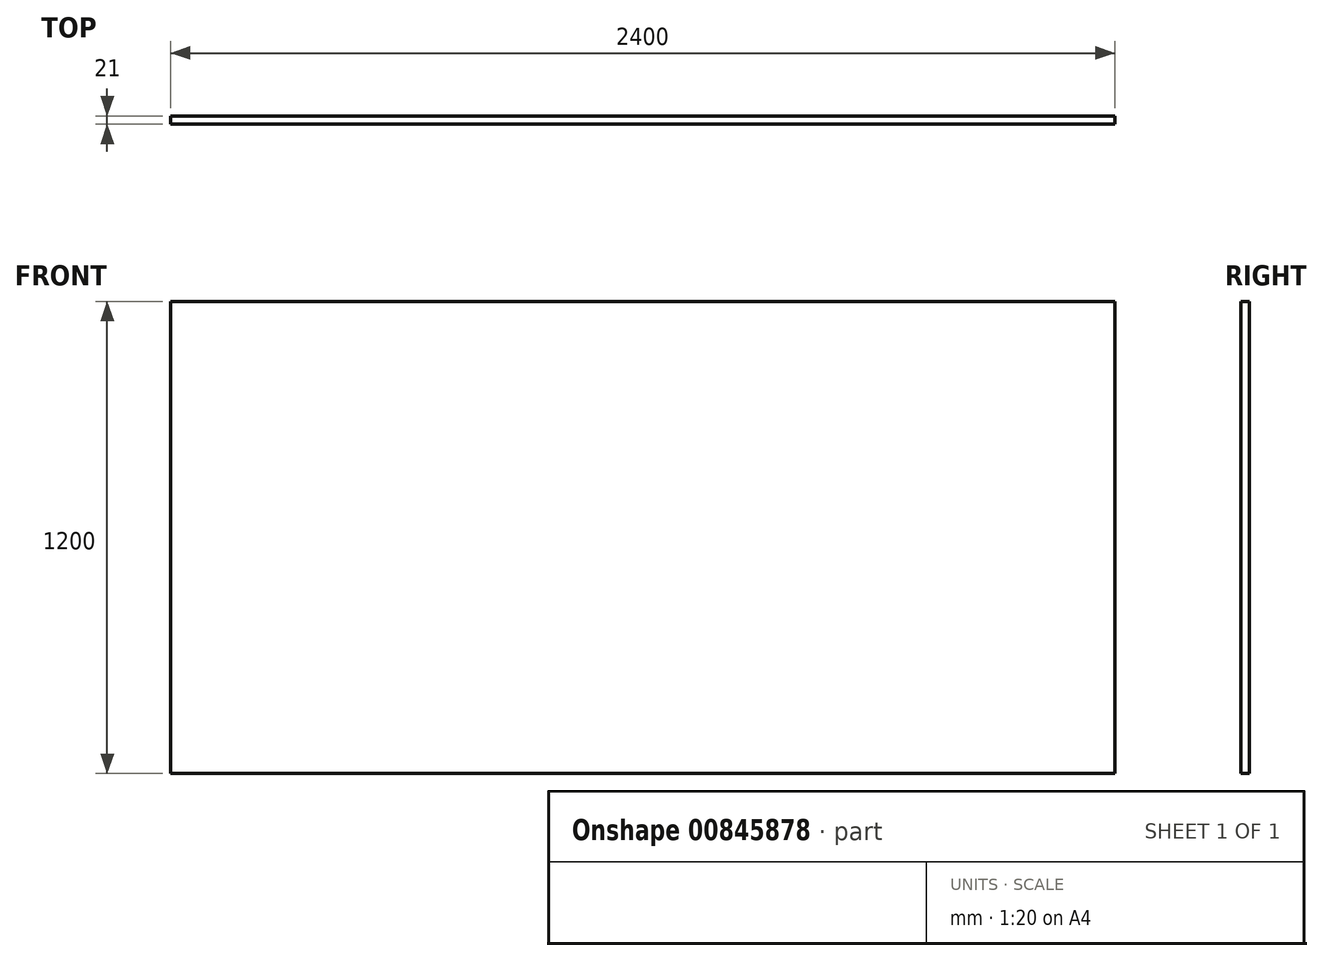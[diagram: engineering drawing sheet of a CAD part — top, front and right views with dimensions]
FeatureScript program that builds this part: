
annotation { "Feature Type Name" : "Feature", "Feature Type Description" : "" }
export const myFeature = defineFeature(function(context is Context, id is Id, definition is map)
    precondition{}
    {
        {
            var Q0;
            Q0=qCreatedBy(makeId("Front.planeOp"),FACE);
            var sketch = newSketch(context, id + "F0", { "sketchPlane" : qUnion([Q0])});
            skLineSegment(sketch, "E0.bottom", {"start": v(1200, -600) * mm, "end": v(-1200, -600) * mm});
            skLineSegment(sketch, "E0.top", {"start": v(1200, 600) * mm, "end": v(-1200, 600) * mm});
            skLineSegment(sketch, "E0.left", {"start": v(1200, -600) * mm, "end": v(1200, 600) * mm});
            skLineSegment(sketch, "E0.right", {"start": v(-1200, -600) * mm, "end": v(-1200, 600) * mm});
            skPoint(sketch, "E0.middle", {"position": v(0, 0) * mm});
            skSolve(sketch);
        }
        {
            var Q0;
            Q0 = qSketchRegion(id + "F0", true);
            extrude(context, id + "F1", {"entities" : qUnion([Q0]), "depth" : 21 * mm, "offsetDistance" : 25 * mm});
        }
    });
